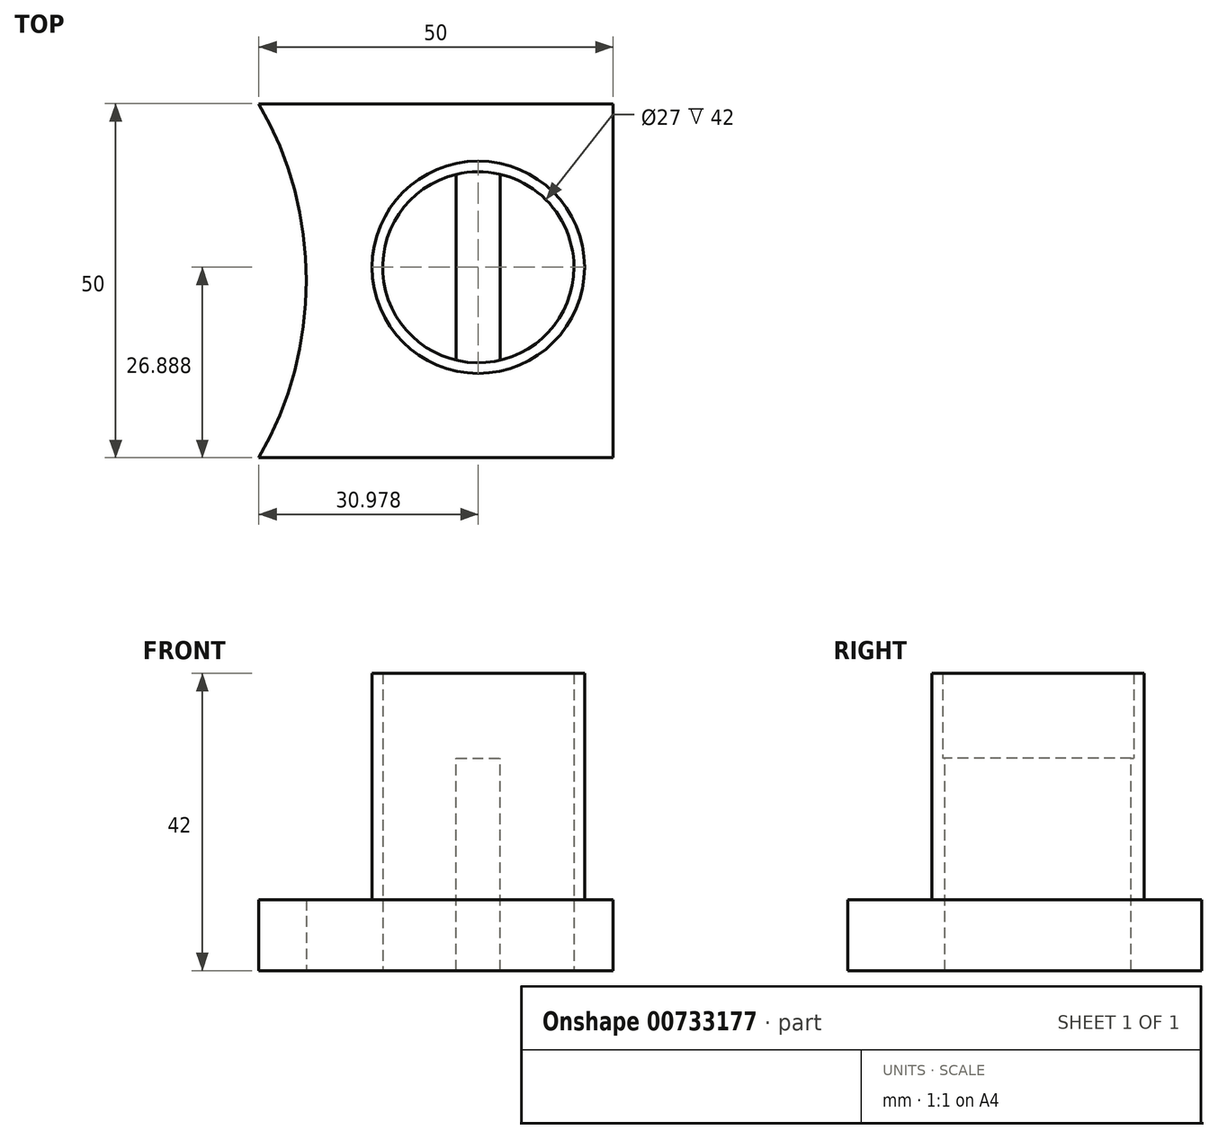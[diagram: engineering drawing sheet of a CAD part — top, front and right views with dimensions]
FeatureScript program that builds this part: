
annotation { "Feature Type Name" : "Feature", "Feature Type Description" : "" }
export const myFeature = defineFeature(function(context is Context, id is Id, definition is map)
    precondition{}
    {
        {
            var Q0;
            Q0=qCreatedBy(makeId("Top.planeOp"),FACE);
            var sketch = newSketch(context, id + "F0", { "sketchPlane" : qUnion([Q0])});
            skLineSegment(sketch, "E0.bottom", {"start": v(-69.71, 60.84) * mm, "end": v(-19.71, 60.84) * mm});
            skLineSegment(sketch, "E0.top", {"start": v(-69.71, 10.84) * mm, "end": v(-19.71, 10.84) * mm});
            skLineSegment(sketch, "E0.right", {"start": v(-19.71, 60.84) * mm, "end": v(-19.71, 10.84) * mm});
            skArc(sketch, "E1", {"start": v(-69.71, 10.84) * mm, "mid": v(-63.01, 35.84) * mm, "end": v(-69.71, 60.84) * mm});
            skSolve(sketch);
        }
        {
            var Q0;
            Q0 = qSketchRegion(id + "F0", true);
            extrude(context, id + "F1", {"entities" : qUnion([Q0]), "depth" : 10 * mm, "offsetDistance" : 25 * mm});
        }
        {
            var Q0;
            Q0=makeQuery(id+"F1.opExtrude","CAP_FACE",FACE,{"disambiguationData":[OSD([sQuery(id+"F0.wireOp",EDGE,"E0.bottom"),sQuery(id+"F0.wireOp",EDGE,"E0.top"),sQuery(id+"F0.wireOp",EDGE,"E0.right"),sQuery(id+"F0.wireOp",EDGE,"E1")])],"isStart":false});
            var sketch = newSketch(context, id + "F2", { "sketchPlane" : qUnion([Q0])});
            skCircle(sketch, "E2", {"center": v(-38.73, 37.73) * mm, "radius": 13.5 * mm});
            skCircle(sketch, "E3", {"center": v(-38.73, 37.73) * mm, "radius": 15 * mm});
            skLineSegment(sketch, "E4", {"start": v(-41.84, 50.87) * mm, "end": v(-41.84, 24.6) * mm});
            skLineSegment(sketch, "E5", {"start": v(-35.62, 50.87) * mm, "end": v(-35.62, 24.6) * mm});
            skSolve(sketch);
        }
        {
            var Q0;
            Q0=makeQuery(id+"F2.imprint","IMPRINT",FACE,{"disambiguationData":[TD([[makeQuery(id+"F2.imprint","IMPRINT",EDGE,{"derivedFrom":sQuery(id+"F2.wireOp",EDGE,"E3")}),1.0]])]});
            extrude(context, id + "F3", {"entities" : qUnion([Q0]), "operationType" : NewBodyOperationType.ADD, "depth" : 32 * mm, "offsetDistance" : 25 * mm});
        }
        {
            var Q0;
            {var subQ0=sQuery(id+"F2.wireOp",EDGE,"E4");Q0=makeQuery(id+"F2.imprint","IMPRINT",FACE,{"disambiguationData":[TD([[makeQuery(id+"F2.imprint","IMPRINT",EDGE,{"derivedFrom":subQ0}),-1.0]])]});}
            var Q1;
            {var subQ0=sQuery(id+"F2.wireOp",EDGE,"E5");Q1=makeQuery(id+"F2.imprint","IMPRINT",FACE,{"disambiguationData":[TD([[makeQuery(id+"F2.imprint","IMPRINT",EDGE,{"derivedFrom":subQ0}),1.0]])]});}
            extrude(context, id + "F4", {"entities" : qUnion([Q0, Q1]), "operationType" : NewBodyOperationType.REMOVE, "oppositeDirection" : true, "depth" : 25 * mm, "offsetDistance" : 25 * mm});
        }
        {
            var Q0;
            Q0=makeQuery(id+"F3.boolean.opBoolean","SPLIT",FACE,{"disambiguationData":[TD([makeQuery(id+"F3.opExtrude","SWEPT_FACE",FACE,{"disambiguationData":[OSD([sQuery(id+"F2.wireOp",EDGE,"E2")])]})])],"derivedFrom":makeQuery(id+"F1.opExtrude","CAP_FACE",FACE,{"disambiguationData":[OSD([sQuery(id+"F0.wireOp",EDGE,"E0.bottom"),sQuery(id+"F0.wireOp",EDGE,"E0.top"),sQuery(id+"F0.wireOp",EDGE,"E0.right"),sQuery(id+"F0.wireOp",EDGE,"E1")])],"isStart":false})});
            extrude(context, id + "F5", {"entities" : qUnion([Q0]), "operationType" : NewBodyOperationType.ADD, "depth" : 20 * mm, "offsetDistance" : 25 * mm});
        }
    });
